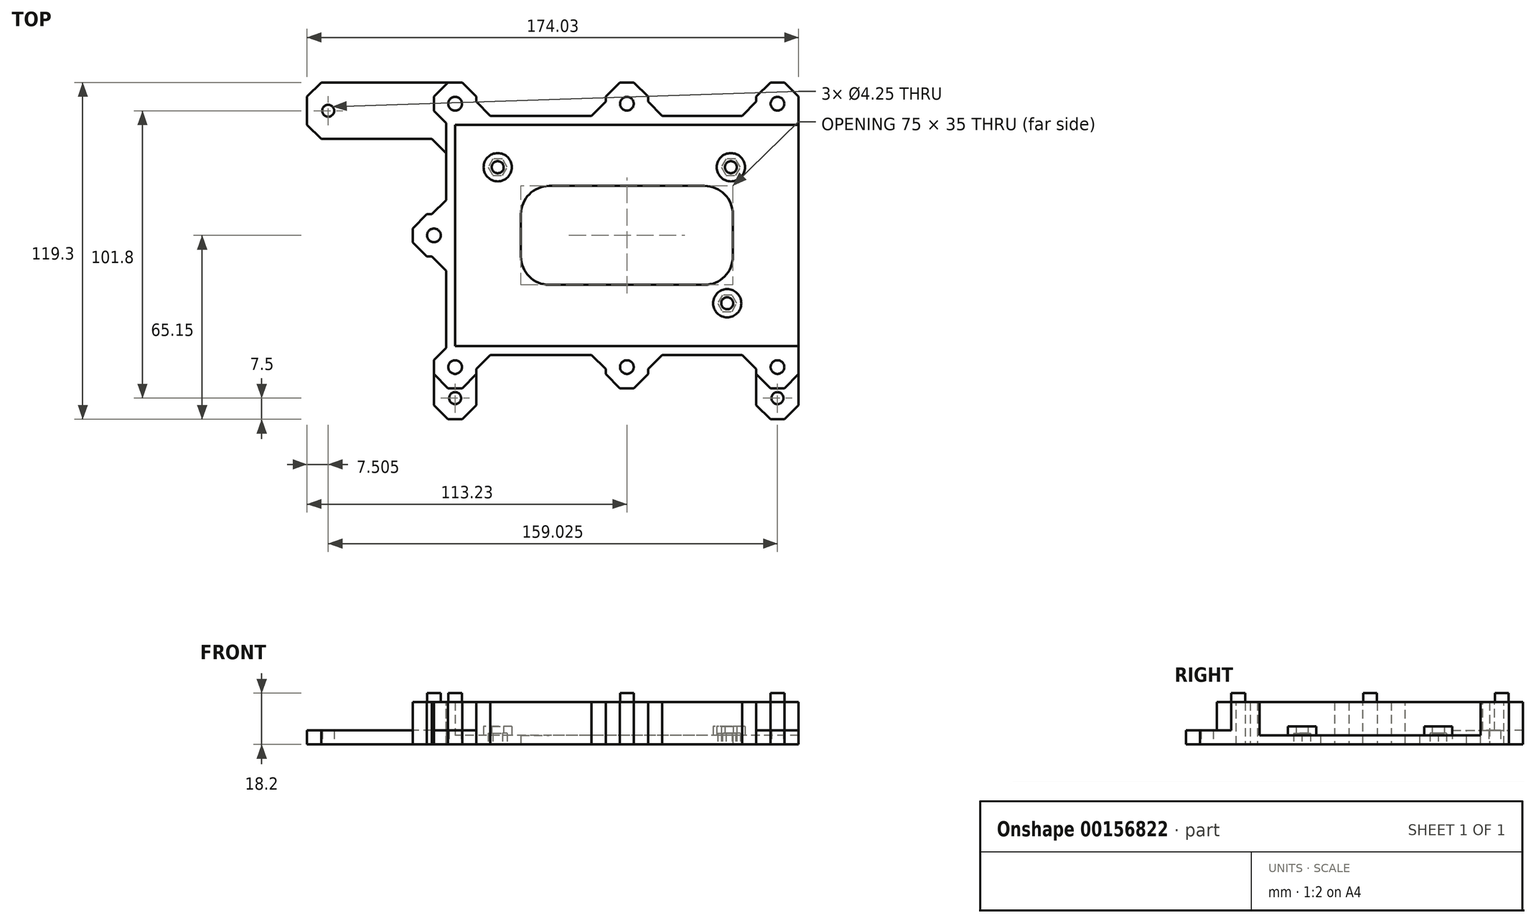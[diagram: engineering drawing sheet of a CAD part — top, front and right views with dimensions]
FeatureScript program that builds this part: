
annotation { "Feature Type Name" : "Feature", "Feature Type Description" : "" }
export const myFeature = defineFeature(function(context is Context, id is Id, definition is map)
    precondition{}
    {
        {
            var Q0;
            Q0=qCreatedBy(makeId("Top.planeOp"),FACE);
            var sketch = newSketch(context, id + "F0", { "sketchPlane" : qUnion([Q0])});
            skLineSegment(sketch, "E0.rect.bottom", {"start": v(50.8, -26.65) * mm, "end": v(-50.8, -26.65) * mm, "construction": true});
            skLineSegment(sketch, "E0.rect.top", {"start": v(50.8, 26.65) * mm, "end": v(-50.8, 26.65) * mm, "construction": true});
            skLineSegment(sketch, "E0.rect.left", {"start": v(50.8, -26.65) * mm, "end": v(50.8, 26.65) * mm, "construction": true});
            skLineSegment(sketch, "E0.rect.right", {"start": v(-50.8, -26.65) * mm, "end": v(-50.8, 26.65) * mm, "construction": true});
            skPoint(sketch, "E0.rect.middle", {"position": v(0, 0) * mm});
            skCircle(sketch, "E1", {"center": v(36.8, 24.15) * mm, "radius": 2.12 * mm});
            skCircle(sketch, "E2", {"center": v(-45.72, 24.15) * mm, "radius": 2.12 * mm});
            skLineSegment(sketch, "E3.rect.bottom", {"start": v(60.8, -39.15) * mm, "end": v(-60.8, -39.15) * mm});
            skLineSegment(sketch, "E3.rect.top", {"start": v(60.8, 39.15) * mm, "end": v(-60.8, 39.15) * mm});
            skLineSegment(sketch, "E3.rect.left", {"start": v(60.8, -39.15) * mm, "end": v(60.8, 39.15) * mm});
            skLineSegment(sketch, "E3.rect.right", {"start": v(-60.8, -39.15) * mm, "end": v(-60.8, 39.15) * mm});
            skLineSegment(sketch, "E4.rect.bottom", {"start": v(27.5, -17.5) * mm, "end": v(-27.5, -17.5) * mm});
            skLineSegment(sketch, "E4.rect.top", {"start": v(27.5, 17.5) * mm, "end": v(-27.5, 17.5) * mm});
            skLineSegment(sketch, "E4.rect.left", {"start": v(37.5, -7.5) * mm, "end": v(37.5, 7.5) * mm});
            skLineSegment(sketch, "E4.rect.right", {"start": v(-37.5, -7.5) * mm, "end": v(-37.5, 7.5) * mm});
            skPoint(sketch, "E5.visualSharp", {"position": v(-37.5, 17.5) * mm});
            skArc(sketch, "E5.filletArc", {"start": v(-27.5, 17.5) * mm, "mid": v(-34.57, 14.57) * mm, "end": v(-37.5, 7.5) * mm});
            skPoint(sketch, "E6.visualSharp", {"position": v(-37.5, -17.5) * mm});
            skArc(sketch, "E6.filletArc", {"start": v(-37.5, -7.5) * mm, "mid": v(-34.57, -14.57) * mm, "end": v(-27.5, -17.5) * mm});
            skPoint(sketch, "E7.visualSharp", {"position": v(37.5, -17.5) * mm});
            skArc(sketch, "E7.filletArc", {"start": v(27.5, -17.5) * mm, "mid": v(34.57, -14.57) * mm, "end": v(37.5, -7.5) * mm});
            skPoint(sketch, "E8.visualSharp", {"position": v(37.5, 17.5) * mm});
            skArc(sketch, "E8.filletArc", {"start": v(37.5, 7.5) * mm, "mid": v(34.57, 14.57) * mm, "end": v(27.5, 17.5) * mm});
            skCircle(sketch, "E9", {"center": v(35.5, -24.05) * mm, "radius": 2.12 * mm});
            skSolve(sketch);
        }
        {
            var Q0;
            Q0=qSketchRegion(id+"F0",true);
            extrude(context, id + "F1", {"entities" : qUnion([Q0]), "depth" : 3.2 * mm});
        }
        {
            var Q0;
            Q0=makeQuery(id+"F1.opExtrude","CAP_FACE",FACE,{"disambiguationData":[OSD([sQuery(id+"F0.wireOp",EDGE,"E1"),sQuery(id+"F0.wireOp",EDGE,"E2"),sQuery(id+"F0.wireOp",EDGE,"427397f8-0dd3-485f-8eed-9c75a59d67ec"),sQuery(id+"F0.wireOp",EDGE,"E3.rect.bottom"),sQuery(id+"F0.wireOp",EDGE,"E3.rect.top"),sQuery(id+"F0.wireOp",EDGE,"E3.rect.left"),sQuery(id+"F0.wireOp",EDGE,"E3.rect.right"),sQuery(id+"F0.wireOp",EDGE,"E4.rect.bottom"),sQuery(id+"F0.wireOp",EDGE,"E4.rect.top"),sQuery(id+"F0.wireOp",EDGE,"E4.rect.left"),sQuery(id+"F0.wireOp",EDGE,"E4.rect.right")])],"isStart":false});
            var sketch = newSketch(context, id + "F2", { "sketchPlane" : qUnion([Q0])});
            skCircle(sketch, "E10", {"center": v(-45.72, 24.15) * mm, "radius": 5 * mm});
            skCircle(sketch, "E11", {"center": v(36.8, 24.15) * mm, "radius": 5 * mm});
            skCircle(sketch, "E12", {"center": v(-45.72, 24.15) * mm, "radius": 2.12 * mm});
            skCircle(sketch, "E13", {"center": v(36.8, 24.15) * mm, "radius": 2.12 * mm});
            skLineSegment(sketch, "E14", {"start": v(0, 0) * mm, "end": v(17.05, 0) * mm, "construction": true});
            skCircle(sketch, "E15", {"center": v(35.5, -24.05) * mm, "radius": 5 * mm});
            skCircle(sketch, "E16", {"center": v(35.5, -24.05) * mm, "radius": 2.12 * mm});
            skSolve(sketch);
        }
        {
            var Q0;
            Q0=qSketchRegion(id+"F2",true);
            extrude(context, id + "F3", {"entities" : qUnion([Q0]), "operationType" : NewBodyOperationType.ADD, "depth" : 3.2 * mm});
        }
        {
            var Q0;
            Q0=makeQuery(id+"F1.opExtrude","CAP_FACE",FACE,{"disambiguationData":[OSD([sQuery(id+"F0.wireOp",EDGE,"E1"),sQuery(id+"F0.wireOp",EDGE,"E2"),sQuery(id+"F0.wireOp",EDGE,"427397f8-0dd3-485f-8eed-9c75a59d67ec"),sQuery(id+"F0.wireOp",EDGE,"E3.rect.bottom"),sQuery(id+"F0.wireOp",EDGE,"E3.rect.top"),sQuery(id+"F0.wireOp",EDGE,"E3.rect.left"),sQuery(id+"F0.wireOp",EDGE,"E3.rect.right"),sQuery(id+"F0.wireOp",EDGE,"E4.rect.bottom"),sQuery(id+"F0.wireOp",EDGE,"E4.rect.top"),sQuery(id+"F0.wireOp",EDGE,"E4.rect.left"),sQuery(id+"F0.wireOp",EDGE,"E4.rect.right")])],"isStart":true});
            var sketch = newSketch(context, id + "F4", { "sketchPlane" : qUnion([Q0])});
            skCircle(sketch, "E17.cCircle", {"center": v(-45.72, -24.15) * mm, "radius": 2.93 * mm, "construction": true});
            skLineSegment(sketch, "E17.0", {"start": v(-47.4, -21.23) * mm, "end": v(-44.03, -21.23) * mm});
            skLineSegment(sketch, "E17.1", {"start": v(-44.03, -21.23) * mm, "end": v(-42.34, -24.15) * mm});
            skLineSegment(sketch, "E17.2", {"start": v(-42.34, -24.15) * mm, "end": v(-44.03, -27.08) * mm});
            skLineSegment(sketch, "E17.3", {"start": v(-44.03, -27.08) * mm, "end": v(-47.4, -27.08) * mm});
            skLineSegment(sketch, "E17.4", {"start": v(-47.4, -27.08) * mm, "end": v(-49.1, -24.15) * mm});
            skLineSegment(sketch, "E17.5", {"start": v(-49.1, -24.15) * mm, "end": v(-47.4, -21.23) * mm});
            skPoint(sketch, "E17.0.midPoint", {"position": v(-45.72, -21.23) * mm});
            skCircle(sketch, "E18.cCircle", {"center": v(36.8, -24.15) * mm, "radius": 2.93 * mm, "construction": true});
            skLineSegment(sketch, "E18.0", {"start": v(35.11, -21.22) * mm, "end": v(38.49, -21.22) * mm});
            skLineSegment(sketch, "E18.1", {"start": v(38.49, -21.22) * mm, "end": v(40.18, -24.15) * mm});
            skLineSegment(sketch, "E18.2", {"start": v(40.18, -24.15) * mm, "end": v(38.49, -27.08) * mm});
            skLineSegment(sketch, "E18.3", {"start": v(38.49, -27.07) * mm, "end": v(35.11, -27.07) * mm});
            skLineSegment(sketch, "E18.4", {"start": v(35.11, -27.08) * mm, "end": v(33.42, -24.15) * mm});
            skLineSegment(sketch, "E18.5", {"start": v(33.42, -24.15) * mm, "end": v(35.11, -21.22) * mm});
            skPoint(sketch, "E18.0.midPoint", {"position": v(36.8, -21.23) * mm});
            skCircle(sketch, "E19.cCircle", {"center": v(35.5, 24.05) * mm, "radius": 2.93 * mm, "construction": true});
            skLineSegment(sketch, "E19.0", {"start": v(37.19, 21.12) * mm, "end": v(33.81, 21.12) * mm});
            skLineSegment(sketch, "E19.1", {"start": v(33.81, 21.12) * mm, "end": v(32.12, 24.05) * mm});
            skLineSegment(sketch, "E19.2", {"start": v(32.12, 24.05) * mm, "end": v(33.81, 26.97) * mm});
            skLineSegment(sketch, "E19.3", {"start": v(33.81, 26.97) * mm, "end": v(37.19, 26.97) * mm});
            skLineSegment(sketch, "E19.4", {"start": v(37.19, 26.97) * mm, "end": v(38.88, 24.05) * mm});
            skLineSegment(sketch, "E19.5", {"start": v(38.88, 24.05) * mm, "end": v(37.19, 21.12) * mm});
            skPoint(sketch, "E19.0.midPoint", {"position": v(35.5, 21.12) * mm});
            skSolve(sketch);
        }
        {
            var Q0;
            Q0=qSketchRegion(id+"F4",true);
            extrude(context, id + "F5", {"entities" : qUnion([Q0]), "operationType" : NewBodyOperationType.REMOVE, "oppositeDirection" : true, "depth" : 4 * mm});
        }
        {
            var Q0;
            Q0=qCreatedBy(makeId("Top.planeOp"),FACE);
            var sketch = newSketch(context, id + "F6", { "sketchPlane" : qUnion([Q0])});
            skLineSegment(sketch, "E20", {"start": v(60.8, 39.15) * mm, "end": v(-60.8, 39.15) * mm});
            skLineSegment(sketch, "E21", {"start": v(-60.8, 39.15) * mm, "end": v(-60.8, -39.15) * mm});
            skLineSegment(sketch, "E22", {"start": v(-60.8, -39.15) * mm, "end": v(60.8, -39.15) * mm});
            skLineSegment(sketch, "E23", {"start": v(60.8, -39.15) * mm, "end": v(60.8, -54.15) * mm});
            skLineSegment(sketch, "E24", {"start": v(60.8, -54.15) * mm, "end": v(45.8, -54.15) * mm});
            skLineSegment(sketch, "E25", {"start": v(45.8, -54.15) * mm, "end": v(45.8, -42.35) * mm});
            skLineSegment(sketch, "E26", {"start": v(45.8, -42.35) * mm, "end": v(7.5, -42.35) * mm});
            skLineSegment(sketch, "E27", {"start": v(7.5, -42.35) * mm, "end": v(7.5, -54.15) * mm});
            skLineSegment(sketch, "E28", {"start": v(7.5, -54.15) * mm, "end": v(-7.5, -54.15) * mm});
            skLineSegment(sketch, "E29", {"start": v(-7.5, -54.15) * mm, "end": v(-7.5, -42.35) * mm});
            skLineSegment(sketch, "E30", {"start": v(-7.5, -42.35) * mm, "end": v(-53.3, -42.35) * mm});
            skLineSegment(sketch, "E31", {"start": v(-53.3, -42.35) * mm, "end": v(-53.3, -54.15) * mm});
            skLineSegment(sketch, "E32", {"start": v(-53.3, -54.15) * mm, "end": v(-68.3, -54.15) * mm});
            skLineSegment(sketch, "E33", {"start": v(-68.3, -54.15) * mm, "end": v(-68.3, -39.15) * mm});
            skLineSegment(sketch, "E34", {"start": v(-68.3, -39.15) * mm, "end": v(-64, -39.15) * mm});
            skLineSegment(sketch, "E35", {"start": v(-64, -39.15) * mm, "end": v(-64, -7.5) * mm});
            skLineSegment(sketch, "E36", {"start": v(-64, -7.5) * mm, "end": v(-75.8, -7.5) * mm});
            skLineSegment(sketch, "E37", {"start": v(-75.8, -7.5) * mm, "end": v(-75.8, 7.5) * mm});
            skLineSegment(sketch, "E38", {"start": v(-75.8, 7.5) * mm, "end": v(-64, 7.5) * mm});
            skLineSegment(sketch, "E39", {"start": v(-64, 7.5) * mm, "end": v(-64, 39.15) * mm});
            skLineSegment(sketch, "E40", {"start": v(-64, 39.15) * mm, "end": v(-68.3, 39.15) * mm});
            skLineSegment(sketch, "E41", {"start": v(-68.3, 39.15) * mm, "end": v(-68.3, 54.15) * mm});
            skLineSegment(sketch, "E42", {"start": v(-68.3, 54.15) * mm, "end": v(-53.3, 54.15) * mm});
            skLineSegment(sketch, "E43", {"start": v(-53.3, 54.15) * mm, "end": v(-53.3, 42.35) * mm});
            skLineSegment(sketch, "E44", {"start": v(-53.3, 42.35) * mm, "end": v(-7.5, 42.35) * mm});
            skLineSegment(sketch, "E45", {"start": v(-7.5, 42.35) * mm, "end": v(-7.5, 54.15) * mm});
            skLineSegment(sketch, "E46", {"start": v(-7.5, 54.15) * mm, "end": v(7.5, 54.15) * mm});
            skLineSegment(sketch, "E47", {"start": v(7.5, 54.15) * mm, "end": v(7.5, 42.35) * mm});
            skLineSegment(sketch, "E48", {"start": v(7.5, 42.35) * mm, "end": v(45.8, 42.35) * mm});
            skLineSegment(sketch, "E49", {"start": v(45.8, 42.35) * mm, "end": v(45.8, 54.15) * mm});
            skLineSegment(sketch, "E50", {"start": v(45.8, 54.15) * mm, "end": v(60.8, 54.15) * mm});
            skLineSegment(sketch, "E51", {"start": v(60.8, 54.15) * mm, "end": v(60.8, 39.15) * mm});
            skSolve(sketch);
        }
        {
            var Q0;
            Q0=qSketchRegion(id+"F6",true);
            extrude(context, id + "F7", {"entities" : qUnion([Q0]), "operationType" : NewBodyOperationType.ADD, "depth" : 15 * mm});
        }
        {
            var Q0;
            Q0=makeQuery(id+"F7.opExtrude","CAP_FACE",FACE,{"disambiguationData":[OSD([sQuery(id+"F6.wireOp",EDGE,"E20"),sQuery(id+"F6.wireOp",EDGE,"E21"),sQuery(id+"F6.wireOp",EDGE,"E22"),sQuery(id+"F6.wireOp",EDGE,"E23"),sQuery(id+"F6.wireOp",EDGE,"E24"),sQuery(id+"F6.wireOp",EDGE,"E25"),sQuery(id+"F6.wireOp",EDGE,"E26"),sQuery(id+"F6.wireOp",EDGE,"E27"),sQuery(id+"F6.wireOp",EDGE,"E28"),sQuery(id+"F6.wireOp",EDGE,"E29"),sQuery(id+"F6.wireOp",EDGE,"E30"),sQuery(id+"F6.wireOp",EDGE,"E31"),sQuery(id+"F6.wireOp",EDGE,"E32"),sQuery(id+"F6.wireOp",EDGE,"E33"),sQuery(id+"F6.wireOp",EDGE,"E34"),sQuery(id+"F6.wireOp",EDGE,"E35"),sQuery(id+"F6.wireOp",EDGE,"E36"),sQuery(id+"F6.wireOp",EDGE,"E37"),sQuery(id+"F6.wireOp",EDGE,"E38"),sQuery(id+"F6.wireOp",EDGE,"E39"),sQuery(id+"F6.wireOp",EDGE,"E40"),sQuery(id+"F6.wireOp",EDGE,"E41"),sQuery(id+"F6.wireOp",EDGE,"E42"),sQuery(id+"F6.wireOp",EDGE,"E43"),sQuery(id+"F6.wireOp",EDGE,"E44"),sQuery(id+"F6.wireOp",EDGE,"E45"),sQuery(id+"F6.wireOp",EDGE,"E46"),sQuery(id+"F6.wireOp",EDGE,"E47"),sQuery(id+"F6.wireOp",EDGE,"E48"),sQuery(id+"F6.wireOp",EDGE,"E49"),sQuery(id+"F6.wireOp",EDGE,"E50"),sQuery(id+"F6.wireOp",EDGE,"E51")])],"isStart":false});
            var sketch = newSketch(context, id + "F8", { "sketchPlane" : qUnion([Q0])});
            skCircle(sketch, "E52", {"center": v(53.3, 46.65) * mm, "radius": 2.43 * mm});
            skCircle(sketch, "E53", {"center": v(0, 46.65) * mm, "radius": 2.43 * mm});
            skCircle(sketch, "E54", {"center": v(-60.8, 46.65) * mm, "radius": 2.43 * mm});
            skCircle(sketch, "E55", {"center": v(-68.3, 0) * mm, "radius": 2.43 * mm});
            skLineSegment(sketch, "E56", {"start": v(0, 0) * mm, "end": v(61.66, 0) * mm, "construction": true});
            skCircle(sketch, "E57.MirrorC", {"center": v(-60.8, -46.65) * mm, "radius": 2.43 * mm});
            skCircle(sketch, "E58.MirrorC", {"center": v(0, -46.65) * mm, "radius": 2.43 * mm});
            skCircle(sketch, "E59.MirrorC", {"center": v(53.3, -46.65) * mm, "radius": 2.43 * mm});
            skSolve(sketch);
        }
        {
            var Q0;
            Q0=qSketchRegion(id+"F8",true);
            extrude(context, id + "F9", {"entities" : qUnion([Q0]), "operationType" : NewBodyOperationType.ADD, "depth" : 3.2 * mm});
        }
        {
            var Q0;
            Q0=makeQuery(id+"F7.opExtrude","SWEPT_EDGE",EDGE,{"disambiguationData":[OSD([sQuery(id+"F6.wireOp",EDGE,"E36"),sQuery(id+"F6.wireOp",EDGE,"E37")])]});
            var Q1;
            Q1=makeQuery(id+"F7.opExtrude","SWEPT_EDGE",EDGE,{"disambiguationData":[OSD([sQuery(id+"F6.wireOp",EDGE,"E37"),sQuery(id+"F6.wireOp",EDGE,"E38")])]});
            var Q2;
            Q2=makeQuery(id+"F7.opExtrude","SWEPT_EDGE",EDGE,{"disambiguationData":[OSD([sQuery(id+"F6.wireOp",EDGE,"E41"),sQuery(id+"F6.wireOp",EDGE,"E42")])]});
            var Q3;
            Q3=makeQuery(id+"F7.opExtrude","SWEPT_EDGE",EDGE,{"disambiguationData":[OSD([sQuery(id+"F6.wireOp",EDGE,"E42"),sQuery(id+"F6.wireOp",EDGE,"E43")])]});
            var Q4;
            Q4=makeQuery(id+"F7.opExtrude","SWEPT_EDGE",EDGE,{"disambiguationData":[OSD([sQuery(id+"F6.wireOp",EDGE,"E45"),sQuery(id+"F6.wireOp",EDGE,"E46")])]});
            var Q5;
            Q5=makeQuery(id+"F7.opExtrude","SWEPT_EDGE",EDGE,{"disambiguationData":[OSD([sQuery(id+"F6.wireOp",EDGE,"E46"),sQuery(id+"F6.wireOp",EDGE,"E47")])]});
            var Q6;
            Q6=makeQuery(id+"F7.opExtrude","SWEPT_EDGE",EDGE,{"disambiguationData":[OSD([sQuery(id+"F6.wireOp",EDGE,"E49"),sQuery(id+"F6.wireOp",EDGE,"E50")])]});
            var Q7;
            Q7=makeQuery(id+"F7.opExtrude","SWEPT_EDGE",EDGE,{"disambiguationData":[OSD([sQuery(id+"F6.wireOp",EDGE,"E50"),sQuery(id+"F6.wireOp",EDGE,"E51")])]});
            var Q8;
            Q8=makeQuery(id+"F7.opExtrude","SWEPT_EDGE",EDGE,{"disambiguationData":[OSD([sQuery(id+"F6.wireOp",EDGE,"E23"),sQuery(id+"F6.wireOp",EDGE,"E24")])]});
            var Q9;
            Q9=makeQuery(id+"F7.opExtrude","SWEPT_EDGE",EDGE,{"disambiguationData":[OSD([sQuery(id+"F6.wireOp",EDGE,"E24"),sQuery(id+"F6.wireOp",EDGE,"E25")])]});
            var Q10;
            Q10=makeQuery(id+"F7.opExtrude","SWEPT_EDGE",EDGE,{"disambiguationData":[OSD([sQuery(id+"F6.wireOp",EDGE,"E27"),sQuery(id+"F6.wireOp",EDGE,"E28")])]});
            var Q11;
            Q11=makeQuery(id+"F7.opExtrude","SWEPT_EDGE",EDGE,{"disambiguationData":[OSD([sQuery(id+"F6.wireOp",EDGE,"E28"),sQuery(id+"F6.wireOp",EDGE,"E29")])]});
            var Q12;
            Q12=makeQuery(id+"F7.opExtrude","SWEPT_EDGE",EDGE,{"disambiguationData":[OSD([sQuery(id+"F6.wireOp",EDGE,"E31"),sQuery(id+"F6.wireOp",EDGE,"E32")])]});
            var Q13;
            Q13=makeQuery(id+"F7.opExtrude","SWEPT_EDGE",EDGE,{"disambiguationData":[OSD([sQuery(id+"F6.wireOp",EDGE,"E32"),sQuery(id+"F6.wireOp",EDGE,"E33")])]});
            var Q14;
            Q14=makeQuery(id+"F7.opExtrude","SWEPT_EDGE",EDGE,{"disambiguationData":[OSD([sQuery(id+"F6.wireOp",EDGE,"E40"),sQuery(id+"F6.wireOp",EDGE,"E41")])]});
            var Q15;
            Q15=makeQuery(id+"F7.opExtrude","SWEPT_EDGE",EDGE,{"disambiguationData":[OSD([sQuery(id+"F6.wireOp",EDGE,"E33"),sQuery(id+"F6.wireOp",EDGE,"E34")])]});
            var Q16;
            Q16=makeQuery(id+"F7.opExtrude","SWEPT_EDGE",EDGE,{"disambiguationData":[OSD([sQuery(id+"F6.wireOp",EDGE,"E29"),sQuery(id+"F6.wireOp",EDGE,"E30")])]});
            var Q17;
            Q17=makeQuery(id+"F7.opExtrude","SWEPT_EDGE",EDGE,{"disambiguationData":[OSD([sQuery(id+"F6.wireOp",EDGE,"E26"),sQuery(id+"F6.wireOp",EDGE,"E27")])]});
            var Q18;
            Q18=makeQuery(id+"F7.opExtrude","SWEPT_EDGE",EDGE,{"disambiguationData":[OSD([sQuery(id+"F6.wireOp",EDGE,"E25"),sQuery(id+"F6.wireOp",EDGE,"E26")])]});
            var Q19;
            Q19=makeQuery(id+"F7.opExtrude","SWEPT_EDGE",EDGE,{"disambiguationData":[OSD([sQuery(id+"F6.wireOp",EDGE,"E30"),sQuery(id+"F6.wireOp",EDGE,"E31")])]});
            var Q20;
            Q20=makeQuery(id+"F7.opExtrude","SWEPT_EDGE",EDGE,{"disambiguationData":[OSD([sQuery(id+"F6.wireOp",EDGE,"E35"),sQuery(id+"F6.wireOp",EDGE,"E36")])]});
            var Q21;
            Q21=makeQuery(id+"F7.opExtrude","SWEPT_EDGE",EDGE,{"disambiguationData":[OSD([sQuery(id+"F6.wireOp",EDGE,"E38"),sQuery(id+"F6.wireOp",EDGE,"E39")])]});
            var Q22;
            Q22=makeQuery(id+"F7.opExtrude","SWEPT_EDGE",EDGE,{"disambiguationData":[OSD([sQuery(id+"F6.wireOp",EDGE,"E43"),sQuery(id+"F6.wireOp",EDGE,"E44")])]});
            var Q23;
            Q23=makeQuery(id+"F7.opExtrude","SWEPT_EDGE",EDGE,{"disambiguationData":[OSD([sQuery(id+"F6.wireOp",EDGE,"E44"),sQuery(id+"F6.wireOp",EDGE,"E45")])]});
            var Q24;
            Q24=makeQuery(id+"F7.opExtrude","SWEPT_EDGE",EDGE,{"disambiguationData":[OSD([sQuery(id+"F6.wireOp",EDGE,"E48"),sQuery(id+"F6.wireOp",EDGE,"E49")])]});
            var Q25;
            Q25=makeQuery(id+"F7.opExtrude","SWEPT_EDGE",EDGE,{"disambiguationData":[OSD([sQuery(id+"F6.wireOp",EDGE,"E47"),sQuery(id+"F6.wireOp",EDGE,"E48")])]});
            chamfer(context, id + "F10", {"entities" : qUnion([Q0, Q1, Q2, Q3, Q4, Q5, Q6, Q7, Q8, Q9, Q10, Q11, Q12, Q13, Q14, Q15, Q16, Q17, Q18, Q19, Q20, Q21, Q22, Q23, Q24, Q25]), "width" : 5 * mm, "tangentPropagation" : true});
        }
        {
            var Q0;
            Q0=qCreatedBy(makeId("Top.planeOp"),FACE);
            var sketch = newSketch(context, id + "F11", { "sketchPlane" : qUnion([Q0])});
            skLineSegment(sketch, "E60.bottom", {"start": v(-53.3, 47.35) * mm, "end": v(-68.3, 47.35) * mm, "construction": true});
            skLineSegment(sketch, "E60.top", {"start": v(-53.3, 65.15) * mm, "end": v(-68.3, 65.15) * mm, "construction": true});
            skLineSegment(sketch, "E60.left", {"start": v(-53.3, 47.35) * mm, "end": v(-53.3, 65.15) * mm, "construction": true});
            skLineSegment(sketch, "E60.right", {"start": v(-68.3, 47.35) * mm, "end": v(-68.3, 65.15) * mm, "construction": true});
            skPoint(sketch, "E60.middle", {"position": v(-60.8, 56.25) * mm});
            skCircle(sketch, "E61", {"center": v(-60.8, 57.65) * mm, "radius": 2.12 * mm, "construction": true});
            skLineSegment(sketch, "E62.bottom", {"start": v(60.8, 47.35) * mm, "end": v(45.8, 47.35) * mm, "construction": true});
            skLineSegment(sketch, "E62.top", {"start": v(60.8, 65.15) * mm, "end": v(45.8, 65.15) * mm, "construction": true});
            skLineSegment(sketch, "E62.left", {"start": v(60.8, 47.35) * mm, "end": v(60.8, 65.15) * mm, "construction": true});
            skLineSegment(sketch, "E62.right", {"start": v(45.8, 47.35) * mm, "end": v(45.8, 65.15) * mm, "construction": true});
            skPoint(sketch, "E62.middle", {"position": v(53.3, 56.25) * mm});
            skCircle(sketch, "E63", {"center": v(53.3, 57.65) * mm, "radius": 2.12 * mm, "construction": true});
            skLineSegment(sketch, "E64", {"start": v(0, 0) * mm, "end": v(61.36, 0) * mm, "construction": true});
            skCircle(sketch, "E65", {"center": v(-60.8, 57.65) * mm, "radius": 3.25 * mm, "construction": true});
            skCircle(sketch, "E66.MirrorC", {"center": v(-60.8, -57.65) * mm, "radius": 2.12 * mm});
            skLineSegment(sketch, "E67.MirrorCS", {"start": v(60.8, -65.15) * mm, "end": v(45.8, -65.15) * mm});
            skLineSegment(sketch, "E68.MirrorCS", {"start": v(-53.3, -65.15) * mm, "end": v(-68.3, -65.15) * mm});
            skCircle(sketch, "E69.MirrorC", {"center": v(53.3, -57.65) * mm, "radius": 2.12 * mm});
            skCircle(sketch, "E70.MirrorC", {"center": v(-60.8, -57.65) * mm, "radius": 3.25 * mm, "construction": true});
            skPoint(sketch, "E71.MirrorP", {"position": v(53.3, -56.25) * mm});
            skPoint(sketch, "E72.MirrorP", {"position": v(-60.8, -56.25) * mm});
            skLineSegment(sketch, "E73.MirrorCS", {"start": v(60.8, -47.35) * mm, "end": v(60.8, -65.15) * mm});
            skLineSegment(sketch, "E74.MirrorCS", {"start": v(45.8, -47.35) * mm, "end": v(45.8, -65.15) * mm});
            skLineSegment(sketch, "E75.MirrorCS", {"start": v(-53.3, -47.35) * mm, "end": v(-53.3, -65.15) * mm});
            skLineSegment(sketch, "E76.MirrorCS", {"start": v(-68.3, -47.35) * mm, "end": v(-68.3, -65.15) * mm});
            skLineSegment(sketch, "E77.MirrorCS", {"start": v(60.8, -47.35) * mm, "end": v(45.8, -47.35) * mm});
            skLineSegment(sketch, "E78.MirrorCS", {"start": v(-53.3, -47.35) * mm, "end": v(-68.3, -47.35) * mm});
            skLineSegment(sketch, "E79.bottom", {"start": v(-63.23, 34.15) * mm, "end": v(-113.23, 34.15) * mm});
            skLineSegment(sketch, "E79.top", {"start": v(-63.23, 54.15) * mm, "end": v(-113.23, 54.15) * mm});
            skLineSegment(sketch, "E79.left", {"start": v(-63.23, 34.15) * mm, "end": v(-63.23, 54.15) * mm});
            skLineSegment(sketch, "E79.right", {"start": v(-113.23, 34.15) * mm, "end": v(-113.23, 54.15) * mm});
            skCircle(sketch, "E80", {"center": v(-105.73, 44.15) * mm, "radius": 2.12 * mm});
            skSolve(sketch);
        }
        {
            var Q0;
            Q0=qSketchRegion(id+"F11",true);
            extrude(context, id + "F12", {"entities" : qUnion([Q0]), "operationType" : NewBodyOperationType.ADD, "depth" : 5 * mm});
        }
        {
            var Q0;
            {var subQ19=sQuery(id+"F11.wireOp",EDGE,"eqWCjPbX-htDR-C8ga-Of8s-fPPzDfkzrk7Z.right");var subQ20=sQuery(id+"F11.wireOp",EDGE,"eqWCjPbX-htDR-C8ga-Of8s-fPPzDfkzrk7Z.top");Q0=makeQuery(id+"F12.boolean.opBoolean","SPLIT",EDGE,{"disambiguationData":[TD([makeQuery(id+"F12.opExtrude","CAP_FACE",FACE,{"disambiguationData":[OSD([sQuery(id+"F11.wireOp",EDGE,"jk3RAOnG-DA1z-41IM-KuVU-WPvvxcmoacko.bottom"),sQuery(id+"F11.wireOp",EDGE,"jk3RAOnG-DA1z-41IM-KuVU-WPvvxcmoacko.top"),sQuery(id+"F11.wireOp",EDGE,"jk3RAOnG-DA1z-41IM-KuVU-WPvvxcmoacko.left"),sQuery(id+"F11.wireOp",EDGE,"jk3RAOnG-DA1z-41IM-KuVU-WPvvxcmoacko.right"),sQuery(id+"F11.wireOp",EDGE,"J50HAIJv-iOe3-t8LS-iFIo-mBBWgSaYphRW")])],"isStart":true})])],"derivedFrom":makeQuery(id+"F12.opExtrude","SWEPT_EDGE",EDGE,{"disambiguationData":[OSD([subQ20,subQ19])]})});}
            var Q1;
            Q1=makeQuery(id+"F12.opExtrude","SWEPT_EDGE",EDGE,{"disambiguationData":[OSD([sQuery(id+"F11.wireOp",EDGE,"eqWCjPbX-htDR-C8ga-Of8s-fPPzDfkzrk7Z.top"),sQuery(id+"F11.wireOp",EDGE,"eqWCjPbX-htDR-C8ga-Of8s-fPPzDfkzrk7Z.left")])]});
            var Q2;
            Q2=makeQuery(id+"F12.opExtrude","SWEPT_EDGE",EDGE,{"disambiguationData":[OSD([sQuery(id+"F11.wireOp",EDGE,"eqWCjPbX-htDR-C8ga-Of8s-fPPzDfkzrk7Z.bottom"),sQuery(id+"F11.wireOp",EDGE,"eqWCjPbX-htDR-C8ga-Of8s-fPPzDfkzrk7Z.left")])]});
            var Q3;
            {var subQ18=sQuery(id+"F11.wireOp",EDGE,"eqWCjPbX-htDR-C8ga-Of8s-fPPzDfkzrk7Z.bottom");var subQ20=sQuery(id+"F11.wireOp",EDGE,"eqWCjPbX-htDR-C8ga-Of8s-fPPzDfkzrk7Z.right");Q3=makeQuery(id+"F12.boolean.opBoolean","SPLIT",EDGE,{"disambiguationData":[TD([makeQuery(id+"F12.opExtrude","CAP_FACE",FACE,{"disambiguationData":[OSD([sQuery(id+"F11.wireOp",EDGE,"jk3RAOnG-DA1z-41IM-KuVU-WPvvxcmoacko.bottom"),sQuery(id+"F11.wireOp",EDGE,"jk3RAOnG-DA1z-41IM-KuVU-WPvvxcmoacko.top"),sQuery(id+"F11.wireOp",EDGE,"jk3RAOnG-DA1z-41IM-KuVU-WPvvxcmoacko.left"),sQuery(id+"F11.wireOp",EDGE,"jk3RAOnG-DA1z-41IM-KuVU-WPvvxcmoacko.right"),sQuery(id+"F11.wireOp",EDGE,"J50HAIJv-iOe3-t8LS-iFIo-mBBWgSaYphRW")])],"isStart":true})])],"derivedFrom":makeQuery(id+"F12.opExtrude","SWEPT_EDGE",EDGE,{"disambiguationData":[OSD([subQ18,subQ20])]})});}
            var Q4;
            Q4=makeQuery(id+"F12.opExtrude","SWEPT_EDGE",EDGE,{"disambiguationData":[OSD([sQuery(id+"F11.wireOp",EDGE,"E62.top"),sQuery(id+"F11.wireOp",EDGE,"E62.left")])]});
            var Q5;
            Q5=makeQuery(id+"F12.opExtrude","SWEPT_EDGE",EDGE,{"disambiguationData":[OSD([sQuery(id+"F11.wireOp",EDGE,"E62.top"),sQuery(id+"F11.wireOp",EDGE,"E62.right")])]});
            var Q6;
            Q6=makeQuery(id+"F12.opExtrude","SWEPT_EDGE",EDGE,{"disambiguationData":[OSD([sQuery(id+"F11.wireOp",EDGE,"jk3RAOnG-DA1z-41IM-KuVU-WPvvxcmoacko.top"),sQuery(id+"F11.wireOp",EDGE,"jk3RAOnG-DA1z-41IM-KuVU-WPvvxcmoacko.left")])]});
            var Q7;
            Q7=makeQuery(id+"F12.opExtrude","SWEPT_EDGE",EDGE,{"disambiguationData":[OSD([sQuery(id+"F11.wireOp",EDGE,"jk3RAOnG-DA1z-41IM-KuVU-WPvvxcmoacko.top"),sQuery(id+"F11.wireOp",EDGE,"jk3RAOnG-DA1z-41IM-KuVU-WPvvxcmoacko.right")])]});
            var Q8;
            Q8=makeQuery(id+"F12.opExtrude","SWEPT_EDGE",EDGE,{"disambiguationData":[OSD([sQuery(id+"F11.wireOp",EDGE,"E60.top"),sQuery(id+"F11.wireOp",EDGE,"E60.right")])]});
            var Q9;
            Q9=makeQuery(id+"F12.opExtrude","SWEPT_EDGE",EDGE,{"disambiguationData":[OSD([sQuery(id+"F11.wireOp",EDGE,"E60.top"),sQuery(id+"F11.wireOp",EDGE,"E60.left")])]});
            var Q10;
            Q10=makeQuery(id+"F12.opExtrude","SWEPT_EDGE",EDGE,{"disambiguationData":[OSD([sQuery(id+"F11.wireOp",EDGE,"7W6G90EH-0ySu-CVKN-ljKH-nmCfsKCbzxSo.top"),sQuery(id+"F11.wireOp",EDGE,"7W6G90EH-0ySu-CVKN-ljKH-nmCfsKCbzxSo.right")])]});
            var Q11;
            Q11=makeQuery(id+"F12.opExtrude","SWEPT_EDGE",EDGE,{"disambiguationData":[OSD([sQuery(id+"F11.wireOp",EDGE,"7W6G90EH-0ySu-CVKN-ljKH-nmCfsKCbzxSo.bottom"),sQuery(id+"F11.wireOp",EDGE,"7W6G90EH-0ySu-CVKN-ljKH-nmCfsKCbzxSo.right")])]});
            var Q12;
            Q12=makeQuery(id+"F12.opExtrude","SWEPT_EDGE",EDGE,{"disambiguationData":[OSD([sQuery(id+"F11.wireOp",EDGE,"963d92d2-a4c7-402a-b001-3de9b50f85252.MirrorCS"),sQuery(id+"F11.wireOp",EDGE,"963d92d2-a4c7-402a-b001-3de9b50f85257.MirrorCS")])]});
            var Q13;
            Q13=makeQuery(id+"F12.opExtrude","SWEPT_EDGE",EDGE,{"disambiguationData":[OSD([sQuery(id+"F11.wireOp",EDGE,"963d92d2-a4c7-402a-b001-3de9b50f85252.MirrorCS"),sQuery(id+"F11.wireOp",EDGE,"963d92d2-a4c7-402a-b001-3de9b50f85258.MirrorCS")])]});
            var Q14;
            Q14=makeQuery(id+"F12.opExtrude","SWEPT_EDGE",EDGE,{"disambiguationData":[OSD([sQuery(id+"F11.wireOp",EDGE,"963d92d2-a4c7-402a-b001-3de9b50f852516.MirrorCS"),sQuery(id+"F11.wireOp",EDGE,"963d92d2-a4c7-402a-b001-3de9b50f852517.MirrorCS")])]});
            var Q15;
            Q15=makeQuery(id+"F12.opExtrude","SWEPT_EDGE",EDGE,{"disambiguationData":[OSD([sQuery(id+"F11.wireOp",EDGE,"963d92d2-a4c7-402a-b001-3de9b50f852513.MirrorCS"),sQuery(id+"F11.wireOp",EDGE,"963d92d2-a4c7-402a-b001-3de9b50f852516.MirrorCS")])]});
            var Q16;
            Q16=makeQuery(id+"F12.opExtrude","SWEPT_EDGE",EDGE,{"disambiguationData":[OSD([sQuery(id+"F11.wireOp",EDGE,"963d92d2-a4c7-402a-b001-3de9b50f85255.MirrorCS"),sQuery(id+"F11.wireOp",EDGE,"963d92d2-a4c7-402a-b001-3de9b50f852510.MirrorCS")])]});
            var Q17;
            Q17=makeQuery(id+"F12.opExtrude","SWEPT_EDGE",EDGE,{"disambiguationData":[OSD([sQuery(id+"F11.wireOp",EDGE,"963d92d2-a4c7-402a-b001-3de9b50f852510.MirrorCS"),sQuery(id+"F11.wireOp",EDGE,"963d92d2-a4c7-402a-b001-3de9b50f852512.MirrorCS")])]});
            var Q18;
            {var subQ0=sQuery(id+"F6.wireOp",EDGE,"E35");Q18=makeQuery(id+"F12.boolean.opBoolean","MERGE",EDGE,{"derivedFrom":[makeQuery(id+"F10.opChamfer","BLEND_EDGE",EDGE,{"blendedFrom":[makeQuery(id+"F7.opExtrude","SWEPT_EDGE",EDGE,{"disambiguationData":[OSD([subQ0,sQuery(id+"F6.wireOp",EDGE,"E36")])]}),makeQuery(id+"F7.opExtrude","SWEPT_FACE",FACE,{"disambiguationData":[OSD([subQ0])]})],"blendedInto":[makeQuery(id+"F7.opExtrude","SWEPT_FACE",FACE,{"disambiguationData":[OSD([subQ0])]})]}),makeQuery(id+"F12.opExtrude","SWEPT_EDGE",EDGE,{"disambiguationData":[OSD([sQuery(id+"F11.wireOp",EDGE,"7W6G90EH-0ySu-CVKN-ljKH-nmCfsKCbzxSo.bottom"),sQuery(id+"F11.wireOp",EDGE,"7W6G90EH-0ySu-CVKN-ljKH-nmCfsKCbzxSo.left")])]})]});}
            var Q19;
            {var subQ0=sQuery(id+"F6.wireOp",EDGE,"E39");Q19=makeQuery(id+"F12.boolean.opBoolean","MERGE",EDGE,{"derivedFrom":[makeQuery(id+"F10.opChamfer","BLEND_EDGE",EDGE,{"blendedFrom":[makeQuery(id+"F7.opExtrude","SWEPT_EDGE",EDGE,{"disambiguationData":[OSD([sQuery(id+"F6.wireOp",EDGE,"E38"),subQ0])]}),makeQuery(id+"F7.opExtrude","SWEPT_FACE",FACE,{"disambiguationData":[OSD([subQ0])]})],"blendedInto":[makeQuery(id+"F7.opExtrude","SWEPT_FACE",FACE,{"disambiguationData":[OSD([subQ0])]})]}),makeQuery(id+"F12.opExtrude","SWEPT_EDGE",EDGE,{"disambiguationData":[OSD([sQuery(id+"F11.wireOp",EDGE,"7W6G90EH-0ySu-CVKN-ljKH-nmCfsKCbzxSo.top"),sQuery(id+"F11.wireOp",EDGE,"7W6G90EH-0ySu-CVKN-ljKH-nmCfsKCbzxSo.left")])]})]});}
            var Q20;
            Q20=makeQuery(id+"F12.opExtrude","SWEPT_EDGE",EDGE,{"disambiguationData":[OSD([sQuery(id+"F11.wireOp",EDGE,"E68.MirrorCS"),sQuery(id+"F11.wireOp",EDGE,"E76.MirrorCS")])]});
            var Q21;
            Q21=makeQuery(id+"F12.opExtrude","SWEPT_EDGE",EDGE,{"disambiguationData":[OSD([sQuery(id+"F11.wireOp",EDGE,"E68.MirrorCS"),sQuery(id+"F11.wireOp",EDGE,"E75.MirrorCS")])]});
            var Q22;
            Q22=makeQuery(id+"F12.opExtrude","SWEPT_EDGE",EDGE,{"disambiguationData":[OSD([sQuery(id+"F11.wireOp",EDGE,"E67.MirrorCS"),sQuery(id+"F11.wireOp",EDGE,"E74.MirrorCS")])]});
            var Q23;
            Q23=makeQuery(id+"F12.opExtrude","SWEPT_EDGE",EDGE,{"disambiguationData":[OSD([sQuery(id+"F11.wireOp",EDGE,"E67.MirrorCS"),sQuery(id+"F11.wireOp",EDGE,"E73.MirrorCS")])]});
            var Q24;
            Q24=makeQuery(id+"F12.opExtrude","SWEPT_EDGE",EDGE,{"disambiguationData":[OSD([sQuery(id+"F11.wireOp",EDGE,"E79.top"),sQuery(id+"F11.wireOp",EDGE,"E79.right")])]});
            var Q25;
            Q25=makeQuery(id+"F12.opExtrude","SWEPT_EDGE",EDGE,{"disambiguationData":[OSD([sQuery(id+"F11.wireOp",EDGE,"E79.bottom"),sQuery(id+"F11.wireOp",EDGE,"E79.right")])]});
            var Q26;
            Q26=makeQuery(id+"F12.boolean.opBoolean","INTERSECT",EDGE,{"derivedFrom":[makeQuery(id+"F7.opExtrude","SWEPT_FACE",FACE,{"disambiguationData":[OSD([sQuery(id+"F6.wireOp",EDGE,"E39")])]}),makeQuery(id+"F12.opExtrude","SWEPT_FACE",FACE,{"disambiguationData":[OSD([sQuery(id+"F11.wireOp",EDGE,"E79.bottom")])]})]});
            chamfer(context, id + "F13", {"entities" : qUnion([Q0, Q1, Q2, Q3, Q4, Q5, Q6, Q7, Q8, Q9, Q10, Q11, Q12, Q13, Q14, Q15, Q16, Q17, Q18, Q19, Q20, Q21, Q22, Q23, Q24, Q25, Q26]), "width" : 5 * mm, "tangentPropagation" : true});
        }
    });
